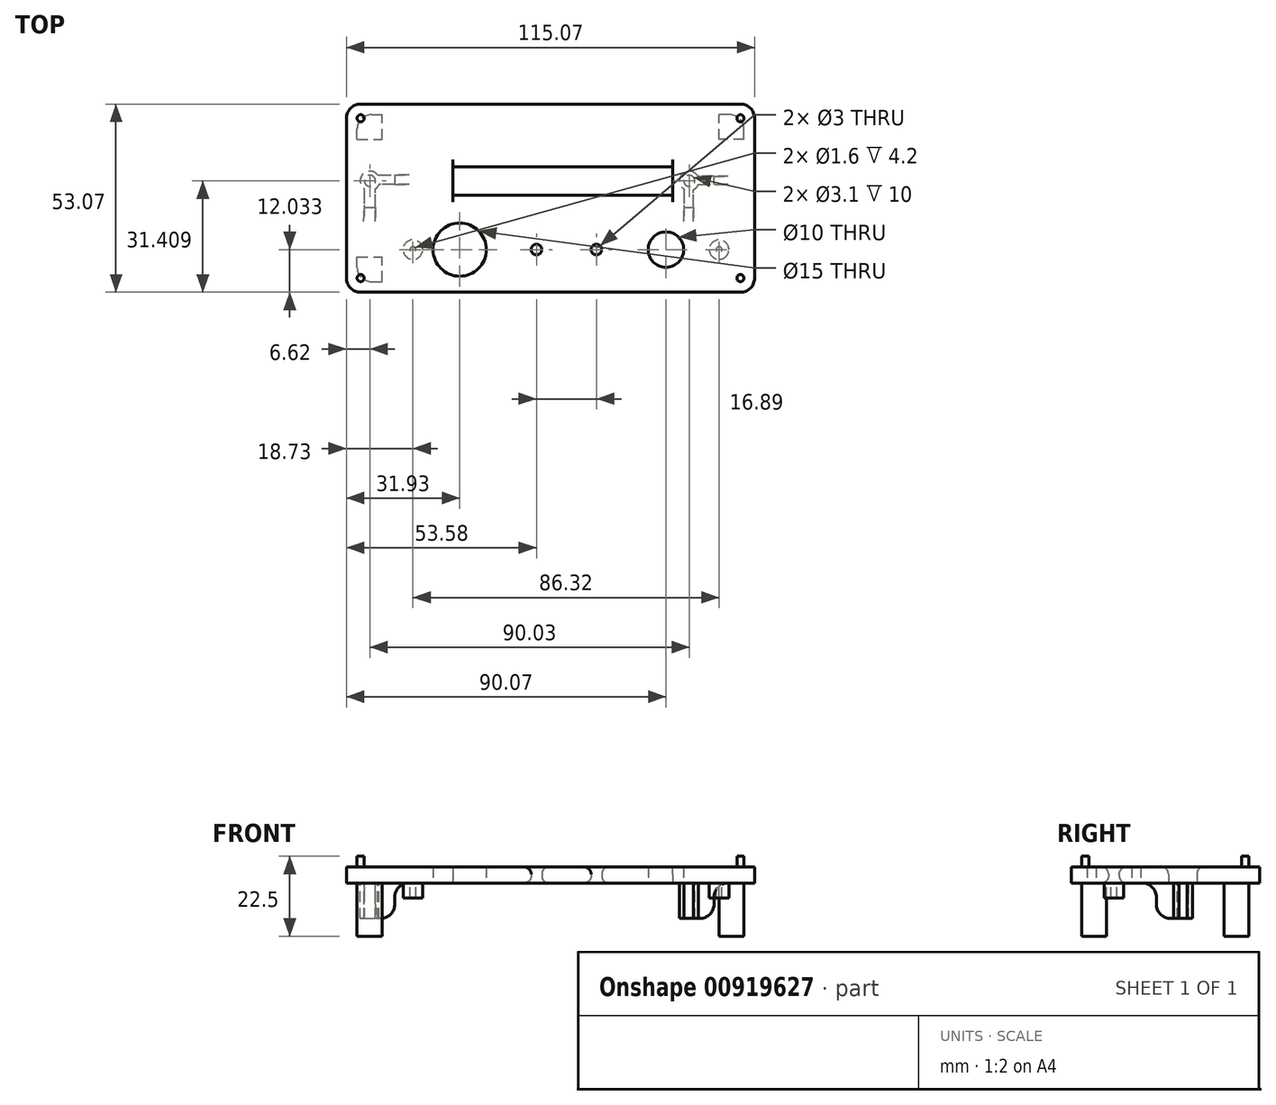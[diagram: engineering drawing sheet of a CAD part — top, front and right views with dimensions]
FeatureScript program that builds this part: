
annotation { "Feature Type Name" : "Feature", "Feature Type Description" : "" }
export const myFeature = defineFeature(function(context is Context, id is Id, definition is map)
    precondition{}
    {
        {
            var Q0;
            Q0=qCreatedBy(makeId("Top.planeOp"),FACE);
            var sketch = newSketch(context, id + "F0", { "sketchPlane" : qUnion([Q0])});
            skLineSegment(sketch, "E0.bottom", {"start": v(-40.47, -4.1) * mm, "end": v(21.53, -4.1) * mm});
            skLineSegment(sketch, "E0.top", {"start": v(-40.47, -12.1) * mm, "end": v(21.53, -12.1) * mm});
            skLineSegment(sketch, "E0.left", {"start": v(-40.47, -4.1) * mm, "end": v(-40.47, -12.1) * mm});
            skLineSegment(sketch, "E0.right", {"start": v(21.53, -4.1) * mm, "end": v(21.53, -12.1) * mm});
            skLineSegment(sketch, "E1.bottom", {"start": v(-70.47, 13.57) * mm, "end": v(44.6, 13.57) * mm});
            skLineSegment(sketch, "E1.left", {"start": v(-70.47, 13.57) * mm, "end": v(-70.47, -39.5) * mm});
            skLineSegment(sketch, "E1.right", {"start": v(44.6, 13.57) * mm, "end": v(44.6, -39.5) * mm});
            skLineSegment(sketch, "E2.top", {"start": v(-70.47, -39.5) * mm, "end": v(44.6, -39.5) * mm});
            skCircle(sketch, "E3", {"center": v(-38.54, -27.47) * mm, "radius": 7.5 * mm});
            skCircle(sketch, "E4", {"center": v(19.6, -27.47) * mm, "radius": 5 * mm});
            skLineSegment(sketch, "E5", {"start": v(-38.54, -27.47) * mm, "end": v(19.6, -27.47) * mm, "construction": true});
            skLineSegment(sketch, "E6", {"start": v(-9.47, -4.1) * mm, "end": v(-9.47, -67.8) * mm, "construction": true});
            skLineSegment(sketch, "E7", {"start": v(-9.47, -27.47) * mm, "end": v(-9.47, -47.05) * mm, "construction": true});
            skCircle(sketch, "E8", {"center": v(-16.89, -27.47) * mm, "radius": 1.5 * mm});
            skCircle(sketch, "E9", {"center": v(0, -27.47) * mm, "radius": 1.5 * mm});
            skSolve(sketch);
        }
        {
            var Q0;
            Q0=qSketchRegion(id+"F0",true);
            extrude(context, id + "F1", {"entities" : qUnion([Q0]), "depth" : 4.5 * mm});
        }
        {
            var Q0;
            Q0=makeQuery(id+"F1.opExtrude","CAP_FACE",FACE,{"disambiguationData":[OSD([sQuery(id+"F0.wireOp",EDGE,"E0.bottom"),sQuery(id+"F0.wireOp",EDGE,"E0.top"),sQuery(id+"F0.wireOp",EDGE,"E0.left"),sQuery(id+"F0.wireOp",EDGE,"E0.right"),sQuery(id+"F0.wireOp",EDGE,"E1.bottom"),sQuery(id+"F0.wireOp",EDGE,"E1.left"),sQuery(id+"F0.wireOp",EDGE,"E1.right"),sQuery(id+"F0.wireOp",EDGE,"E2.top"),sQuery(id+"F0.wireOp",EDGE,"E3"),sQuery(id+"F0.wireOp",EDGE,"E4"),sQuery(id+"F0.wireOp",EDGE,"E8"),sQuery(id+"F0.wireOp",EDGE,"E9")])],"isStart":true});
            var sketch = newSketch(context, id + "F2", { "sketchPlane" : qUnion([Q0])});
            skCircle(sketch, "E10", {"center": v(-51.74, 27.47) * mm, "radius": 2.75 * mm});
            skCircle(sketch, "E11", {"center": v(-51.74, 27.47) * mm, "radius": 0.8 * mm});
            skLineSegment(sketch, "E12", {"start": v(-38.54, 53.37) * mm, "end": v(-38.54, -15.25) * mm, "construction": true});
            skLineSegment(sketch, "E13", {"start": v(19.6, 54.56) * mm, "end": v(19.6, -16.46) * mm, "construction": true});
            skLineSegment(sketch, "E14", {"start": v(-73.52, 27.47) * mm, "end": v(51.35, 27.47) * mm, "construction": true});
            skPoint(sketch, "E15", {"position": v(-38.54, 27.47) * mm});
            skPoint(sketch, "E16", {"position": v(19.6, 27.47) * mm});
            skCircle(sketch, "E17", {"center": v(34.58, 27.47) * mm, "radius": 0.8 * mm});
            skCircle(sketch, "E18", {"center": v(34.58, 27.47) * mm, "radius": 2.75 * mm});
            skLineSegment(sketch, "E19", {"start": v(-73.6, 8.1) * mm, "end": v(49.99, 8.1) * mm, "construction": true});
            skCircle(sketch, "E20", {"center": v(-63.85, 8.1) * mm, "radius": 1.55 * mm});
            skCircle(sketch, "E21", {"center": v(-63.85, 8.1) * mm, "radius": 2.75 * mm});
            skCircle(sketch, "E22", {"center": v(26.18, 8.1) * mm, "radius": 1.55 * mm});
            skCircle(sketch, "E23", {"center": v(26.18, 8.1) * mm, "radius": 2.75 * mm});
            skPoint(sketch, "E24", {"position": v(-40.47, 8.1) * mm});
            skPoint(sketch, "E25", {"position": v(21.53, 8.1) * mm});
            skLineSegment(sketch, "E26.bottom", {"start": v(-67.47, 36.5) * mm, "end": v(-60.47, 36.5) * mm});
            skLineSegment(sketch, "E26.top", {"start": v(-67.47, 29.5) * mm, "end": v(-60.47, 29.5) * mm});
            skLineSegment(sketch, "E26.left", {"start": v(-67.47, 36.5) * mm, "end": v(-67.47, 29.5) * mm});
            skLineSegment(sketch, "E26.right", {"start": v(-60.47, 36.5) * mm, "end": v(-60.47, 29.5) * mm});
            skLineSegment(sketch, "E27.bottom", {"start": v(-67.47, -3.57) * mm, "end": v(-60.47, -3.57) * mm});
            skLineSegment(sketch, "E27.top", {"start": v(-67.47, -10.57) * mm, "end": v(-60.47, -10.57) * mm});
            skLineSegment(sketch, "E27.left", {"start": v(-67.47, -3.57) * mm, "end": v(-67.47, -10.57) * mm});
            skLineSegment(sketch, "E27.right", {"start": v(-60.47, -3.57) * mm, "end": v(-60.47, -10.57) * mm});
            skLineSegment(sketch, "E28.bottom", {"start": v(41.6, -3.57) * mm, "end": v(34.6, -3.57) * mm});
            skLineSegment(sketch, "E28.top", {"start": v(41.6, -10.57) * mm, "end": v(34.6, -10.57) * mm});
            skLineSegment(sketch, "E28.left", {"start": v(41.6, -3.57) * mm, "end": v(41.6, -10.57) * mm});
            skLineSegment(sketch, "E28.right", {"start": v(34.6, -3.57) * mm, "end": v(34.6, -10.57) * mm});
            skLineSegment(sketch, "E29", {"start": v(-65.43, 10.34) * mm, "end": v(-65.51, 15.5) * mm});
            skLineSegment(sketch, "E30", {"start": v(-65.51, 15.5) * mm, "end": v(-62.29, 15.5) * mm});
            skLineSegment(sketch, "E31", {"start": v(-62.29, 15.5) * mm, "end": v(-62.29, 10.35) * mm});
            skLineSegment(sketch, "E32", {"start": v(-61.64, 6.46) * mm, "end": v(-56.85, 6.46) * mm});
            skLineSegment(sketch, "E33", {"start": v(-56.85, 6.46) * mm, "end": v(-56.85, 9.13) * mm});
            skLineSegment(sketch, "E34", {"start": v(-56.85, 9.13) * mm, "end": v(-61.3, 9.13) * mm});
            skLineSegment(sketch, "E35", {"start": v(24.62, 10.35) * mm, "end": v(24.62, 15.5) * mm});
            skPoint(sketch, "E35.endSnap0", {"position": v(-63.9, 15.5) * mm});
            skLineSegment(sketch, "E36", {"start": v(24.62, 15.5) * mm, "end": v(27.31, 15.5) * mm});
            skLineSegment(sketch, "E37", {"start": v(27.31, 15.5) * mm, "end": v(27.31, 10.6) * mm});
            skLineSegment(sketch, "E38", {"start": v(28.73, 9.13) * mm, "end": v(33.17, 9.13) * mm});
            skLineSegment(sketch, "E39", {"start": v(33.17, 9.13) * mm, "end": v(33.17, 6.83) * mm});
            skLineSegment(sketch, "E40", {"start": v(33.17, 6.83) * mm, "end": v(28.62, 6.83) * mm});
            skSolve(sketch);
        }
        {
            var Q0;
            Q0=makeQuery(id+"F2.imprint","IMPRINT",FACE,{"disambiguationData":[TD([[makeQuery(id+"F2.imprint","IMPRINT",EDGE,{"derivedFrom":sQuery(id+"F2.wireOp",EDGE,"E10")}),1.0]])]});
            var Q1;
            Q1=makeQuery(id+"F2.imprint","IMPRINT",FACE,{"disambiguationData":[TD([[makeQuery(id+"F2.imprint","IMPRINT",EDGE,{"derivedFrom":sQuery(id+"F2.wireOp",EDGE,"E17")}),-1.0]])]});
            extrude(context, id + "F3", {"entities" : qUnion([Q0, Q1]), "operationType" : NewBodyOperationType.ADD, "depth" : 4.2 * mm});
        }
        {
            var Q0;
            Q0=makeQuery(id+"F2.imprint","IMPRINT",FACE,{"disambiguationData":[TD([[makeQuery(id+"F2.imprint","IMPRINT",EDGE,{"derivedFrom":sQuery(id+"F2.wireOp",EDGE,"E20")}),-1.0]])]});
            var Q1;
            Q1=makeQuery(id+"F2.imprint","IMPRINT",FACE,{"disambiguationData":[TD([[makeQuery(id+"F2.imprint","IMPRINT",EDGE,{"derivedFrom":sQuery(id+"F2.wireOp",EDGE,"E22")}),-1.0]])]});
            var Q2;
            {var subQ0=sQuery(id+"F2.wireOp",EDGE,"E29");Q2=makeQuery(id+"F2.imprint","IMPRINT",FACE,{"disambiguationData":[TD([[makeQuery(id+"F2.imprint","IMPRINT",EDGE,{"derivedFrom":subQ0}),-1.0]])]});}
            var Q3;
            {var subQ1=sQuery(id+"F2.wireOp",EDGE,"E32");Q3=makeQuery(id+"F2.imprint","IMPRINT",FACE,{"disambiguationData":[TD([[makeQuery(id+"F2.imprint","IMPRINT",EDGE,{"derivedFrom":subQ1}),1.0]])]});}
            var Q4;
            {var subQ1=sQuery(id+"F2.wireOp",EDGE,"E35");Q4=makeQuery(id+"F2.imprint","IMPRINT",FACE,{"disambiguationData":[TD([[makeQuery(id+"F2.imprint","IMPRINT",EDGE,{"derivedFrom":subQ1}),-1.0]])]});}
            var Q5;
            {var subQ1=sQuery(id+"F2.wireOp",EDGE,"E38");Q5=makeQuery(id+"F2.imprint","IMPRINT",FACE,{"disambiguationData":[TD([[makeQuery(id+"F2.imprint","IMPRINT",EDGE,{"derivedFrom":subQ1}),-1.0]])]});}
            extrude(context, id + "F4", {"entities" : qUnion([Q0, Q1, Q2, Q3, Q4, Q5]), "operationType" : NewBodyOperationType.ADD, "depth" : 10 * mm});
        }
        {
            var Q0;
            Q0=makeQuery(id+"F2.imprint","IMPRINT",FACE,{"disambiguationData":[TD([[makeQuery(id+"F2.imprint","IMPRINT",EDGE,{"derivedFrom":sQuery(id+"F2.wireOp",EDGE,"E26.bottom")}),-1.0]])]});
            var Q1;
            Q1=makeQuery(id+"F2.imprint","IMPRINT",FACE,{"disambiguationData":[TD([[makeQuery(id+"F2.imprint","IMPRINT",EDGE,{"derivedFrom":sQuery(id+"F2.wireOp",EDGE,"E28.bottom")}),1.0]])]});
            var Q2;
            Q2=makeQuery(id+"F2.imprint","IMPRINT",FACE,{"disambiguationData":[TD([[makeQuery(id+"F2.imprint","IMPRINT",EDGE,{"derivedFrom":sQuery(id+"F2.wireOp",EDGE,"E27.bottom")}),-1.0]])]});
            extrude(context, id + "F5", {"entities" : qUnion([Q0, Q1, Q2]), "operationType" : NewBodyOperationType.ADD, "depth" : 15 * mm});
        }
        {
            var Q0;
            Q0=makeQuery(id+"F1.opExtrude","SWEPT_EDGE",EDGE,{"disambiguationData":[OSD([sQuery(id+"F0.wireOp",EDGE,"E1.left"),sQuery(id+"F0.wireOp",EDGE,"E2.top")])]});
            var Q1;
            Q1=makeQuery(id+"F1.opExtrude","SWEPT_EDGE",EDGE,{"disambiguationData":[OSD([sQuery(id+"F0.wireOp",EDGE,"E1.bottom"),sQuery(id+"F0.wireOp",EDGE,"E1.left")])]});
            var Q2;
            Q2=makeQuery(id+"F5.opExtrude","SWEPT_EDGE",EDGE,{"disambiguationData":[OSD([sQuery(id+"F2.wireOp",EDGE,"E26.bottom"),sQuery(id+"F2.wireOp",EDGE,"E26.left")])]});
            var Q3;
            Q3=makeQuery(id+"F5.opExtrude","SWEPT_EDGE",EDGE,{"disambiguationData":[OSD([sQuery(id+"F2.wireOp",EDGE,"E27.top"),sQuery(id+"F2.wireOp",EDGE,"E27.left")])]});
            var Q4;
            Q4=makeQuery(id+"F5.opExtrude","SWEPT_EDGE",EDGE,{"disambiguationData":[OSD([sQuery(id+"F2.wireOp",EDGE,"E28.top"),sQuery(id+"F2.wireOp",EDGE,"E28.left")])]});
            var Q5;
            Q5=makeQuery(id+"F1.opExtrude","SWEPT_EDGE",EDGE,{"disambiguationData":[OSD([sQuery(id+"F0.wireOp",EDGE,"E1.bottom"),sQuery(id+"F0.wireOp",EDGE,"E1.right")])]});
            var Q6;
            Q6=makeQuery(id+"F1.opExtrude","SWEPT_EDGE",EDGE,{"disambiguationData":[OSD([sQuery(id+"F0.wireOp",EDGE,"E1.right"),sQuery(id+"F0.wireOp",EDGE,"E2.top")])]});
            var Q7;
            Q7=makeQuery(id+"F4.opExtrude","CAP_EDGE",EDGE,{"disambiguationData":[OSD([sQuery(id+"F2.wireOp",EDGE,"E30")])],"isStart":true});
            var Q8;
            Q8=makeQuery(id+"F4.opExtrude","CAP_EDGE",EDGE,{"disambiguationData":[OSD([sQuery(id+"F2.wireOp",EDGE,"E33")])],"isStart":true});
            var Q9;
            Q9=makeQuery(id+"F4.opExtrude","CAP_EDGE",EDGE,{"disambiguationData":[OSD([sQuery(id+"F2.wireOp",EDGE,"E30")])],"isStart":false});
            var Q10;
            Q10=makeQuery(id+"F4.opExtrude","CAP_EDGE",EDGE,{"disambiguationData":[OSD([sQuery(id+"F2.wireOp",EDGE,"E33")])],"isStart":false});
            var Q11;
            Q11=makeQuery(id+"F4.opExtrude","CAP_EDGE",EDGE,{"disambiguationData":[OSD([sQuery(id+"F2.wireOp",EDGE,"E36")])],"isStart":false});
            var Q12;
            Q12=makeQuery(id+"F4.opExtrude","CAP_EDGE",EDGE,{"disambiguationData":[OSD([sQuery(id+"F2.wireOp",EDGE,"E36")])],"isStart":true});
            var Q13;
            Q13=makeQuery(id+"F4.opExtrude","CAP_EDGE",EDGE,{"disambiguationData":[OSD([sQuery(id+"F2.wireOp",EDGE,"E39")])],"isStart":false});
            var Q14;
            Q14=makeQuery(id+"F4.opExtrude","CAP_EDGE",EDGE,{"disambiguationData":[OSD([sQuery(id+"F2.wireOp",EDGE,"E39")])],"isStart":true});
            fillet(context, id + "F6", {"entities" : qUnion([Q0, Q1, Q2, Q3, Q4, Q5, Q6, Q7, Q8, Q9, Q10, Q11, Q12, Q13, Q14]), "radius" : 4 * mm, "tangentPropagation" : true, "allowEdgeOverflow" : false});
        }
        {
            var Q0;
            Q0=makeQuery(id+"F3.opExtrude","CAP_EDGE",EDGE,{"disambiguationData":[OSD([sQuery(id+"F2.wireOp",EDGE,"E18")])],"isStart":true});
            var Q1;
            Q1=makeQuery(id+"F3.opExtrude","CAP_EDGE",EDGE,{"disambiguationData":[OSD([sQuery(id+"F2.wireOp",EDGE,"E10")])],"isStart":true});
            var Q2;
            Q2=makeQuery(id+"F5.opExtrude","CAP_EDGE",EDGE,{"disambiguationData":[OSD([sQuery(id+"F2.wireOp",EDGE,"E27.right")])],"isStart":true});
            var Q3;
            Q3=makeQuery(id+"F5.opExtrude","CAP_EDGE",EDGE,{"disambiguationData":[OSD([sQuery(id+"F2.wireOp",EDGE,"E27.bottom")])],"isStart":true});
            var Q4;
            Q4=makeQuery(id+"F5.opExtrude","CAP_EDGE",EDGE,{"disambiguationData":[OSD([sQuery(id+"F2.wireOp",EDGE,"E28.right")])],"isStart":true});
            var Q5;
            Q5=makeQuery(id+"F5.opExtrude","CAP_EDGE",EDGE,{"disambiguationData":[OSD([sQuery(id+"F2.wireOp",EDGE,"E28.bottom")])],"isStart":true});
            var Q6;
            Q6=makeQuery(id+"F5.opExtrude","CAP_EDGE",EDGE,{"disambiguationData":[OSD([sQuery(id+"F2.wireOp",EDGE,"E26.right")])],"isStart":true});
            var Q7;
            Q7=makeQuery(id+"F5.opExtrude","CAP_EDGE",EDGE,{"disambiguationData":[OSD([sQuery(id+"F2.wireOp",EDGE,"E26.top")])],"isStart":true});
            var Q8;
            Q8=makeQuery(id+"F1.opExtrude","CAP_EDGE",EDGE,{"disambiguationData":[OSD([sQuery(id+"F0.wireOp",EDGE,"E0.top")])],"isStart":false});
            var Q9;
            Q9=makeQuery(id+"F1.opExtrude","CAP_EDGE",EDGE,{"disambiguationData":[OSD([sQuery(id+"F0.wireOp",EDGE,"E0.bottom")])],"isStart":false});
            var Q10;
            Q10=makeQuery(id+"F1.opExtrude","CAP_EDGE",EDGE,{"disambiguationData":[OSD([sQuery(id+"F0.wireOp",EDGE,"E9")])],"isStart":false});
            var Q11;
            Q11=makeQuery(id+"F1.opExtrude","CAP_EDGE",EDGE,{"disambiguationData":[OSD([sQuery(id+"F0.wireOp",EDGE,"E8")])],"isStart":false});
            var Q12;
            Q12=makeQuery(id+"F1.opExtrude","CAP_EDGE",EDGE,{"disambiguationData":[OSD([sQuery(id+"F0.wireOp",EDGE,"E9")])],"isStart":true});
            var Q13;
            Q13=makeQuery(id+"F1.opExtrude","CAP_EDGE",EDGE,{"disambiguationData":[OSD([sQuery(id+"F0.wireOp",EDGE,"E8")])],"isStart":true});
            fillet(context, id + "F7", {"entities" : qUnion([Q0, Q1, Q2, Q3, Q4, Q5, Q6, Q7, Q8, Q9, Q10, Q11, Q12, Q13]), "radius" : 2 * mm, "tangentPropagation" : true, "allowEdgeOverflow" : false});
        }
        {
            var Q0;
            Q0=makeQuery(id+"F1.opExtrude","CAP_FACE",FACE,{"disambiguationData":[OSD([sQuery(id+"F0.wireOp",EDGE,"E0.bottom"),sQuery(id+"F0.wireOp",EDGE,"E0.top"),sQuery(id+"F0.wireOp",EDGE,"E0.left"),sQuery(id+"F0.wireOp",EDGE,"E0.right"),sQuery(id+"F0.wireOp",EDGE,"E1.bottom"),sQuery(id+"F0.wireOp",EDGE,"E1.left"),sQuery(id+"F0.wireOp",EDGE,"E1.right"),sQuery(id+"F0.wireOp",EDGE,"E2.top"),sQuery(id+"F0.wireOp",EDGE,"E3"),sQuery(id+"F0.wireOp",EDGE,"E4"),sQuery(id+"F0.wireOp",EDGE,"E8"),sQuery(id+"F0.wireOp",EDGE,"E9")])],"isStart":false});
            var sketch = newSketch(context, id + "F8", { "sketchPlane" : qUnion([Q0])});
            skCircle(sketch, "E41", {"center": v(-66.47, 9.57) * mm, "radius": 1 * mm});
            skCircle(sketch, "E42", {"center": v(40.6, 9.57) * mm, "radius": 1 * mm});
            skCircle(sketch, "E43", {"center": v(40.6, -35.5) * mm, "radius": 1 * mm});
            skCircle(sketch, "E44", {"center": v(-66.47, -35.5) * mm, "radius": 1 * mm});
            skSolve(sketch);
        }
        {
            var Q0;
            Q0=qSketchRegion(id+"F8",true);
            extrude(context, id + "F9", {"entities" : qUnion([Q0]), "operationType" : NewBodyOperationType.ADD, "depth" : 3 * mm});
        }
    });
